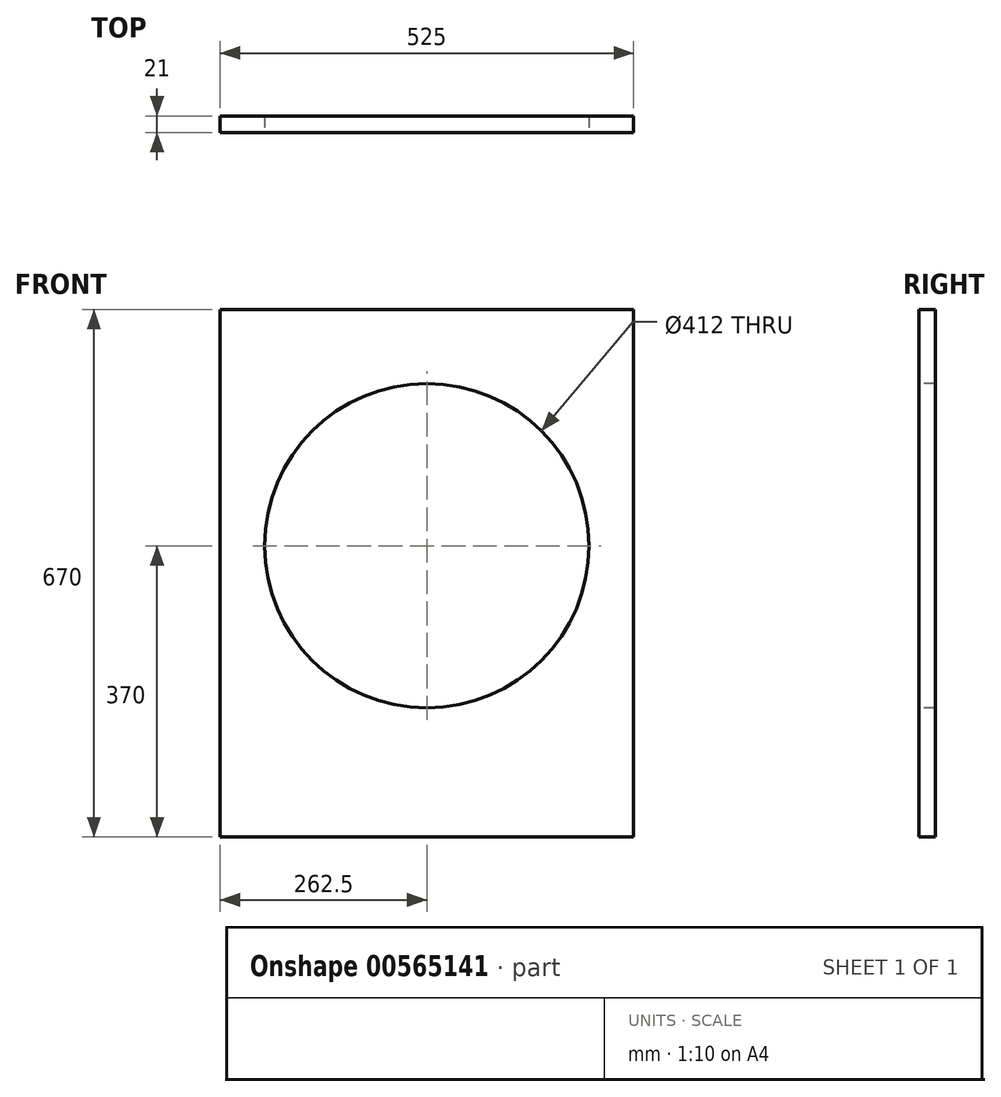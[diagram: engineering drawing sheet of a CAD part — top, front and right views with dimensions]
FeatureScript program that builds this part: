
annotation { "Feature Type Name" : "Feature", "Feature Type Description" : "" }
export const myFeature = defineFeature(function(context is Context, id is Id, definition is map)
    precondition{}
    {
        {
            var Q0;
            Q0=qCreatedBy(makeId("Front.planeOp"),FACE);
            var sketch = newSketch(context, id + "F0", { "sketchPlane" : qUnion([Q0])});
            skLineSegment(sketch, "E0.bottom", {"start": v(262.5, 335) * mm, "end": v(-262.5, 335) * mm});
            skLineSegment(sketch, "E0.top", {"start": v(262.5, -335) * mm, "end": v(-262.5, -335) * mm});
            skLineSegment(sketch, "E0.left", {"start": v(262.5, 335) * mm, "end": v(262.5, -335) * mm});
            skLineSegment(sketch, "E0.right", {"start": v(-262.5, 335) * mm, "end": v(-262.5, -335) * mm});
            skPoint(sketch, "E0.middle", {"position": v(0, 0) * mm});
            skSolve(sketch);
        }
        {
            var Q0;
            Q0 = qSketchRegion(id + "F0", true);
            extrude(context, id + "F1", {"entities" : qUnion([Q0]), "depth" : 21 * mm, "offsetDistance" : 25 * mm});
        }
        {
            var Q0;
            Q0=makeQuery(id+"F1.opExtrude","CAP_FACE",FACE,{"disambiguationData":[OSD([sQuery(id+"F0.wireOp",EDGE,"E0.bottom"),sQuery(id+"F0.wireOp",EDGE,"E0.top"),sQuery(id+"F0.wireOp",EDGE,"E0.left"),sQuery(id+"F0.wireOp",EDGE,"E0.right")])],"isStart":false});
            var sketch = newSketch(context, id + "F2", { "sketchPlane" : qUnion([Q0])});
            skCircle(sketch, "E1", {"center": v(0, 35) * mm, "radius": 206 * mm});
            skPoint(sketch, "E2", {"position": v(0, 241) * mm});
            skPoint(sketch, "E3", {"position": v(0, -171) * mm});
            skSolve(sketch);
        }
        {
            var Q0;
            Q0=makeQuery(id+"F2.imprint","IMPRINT",FACE,{"disambiguationData":[TD([[makeQuery(id+"F2.imprint","IMPRINT",EDGE,{"derivedFrom":sQuery(id+"F2.wireOp",EDGE,"E1")}),1.0]])]});
            extrude(context, id + "F3", {"entities" : qUnion([Q0]), "operationType" : NewBodyOperationType.REMOVE, "oppositeDirection" : true, "depth" : 25 * mm, "offsetDistance" : 25 * mm});
        }
    });
